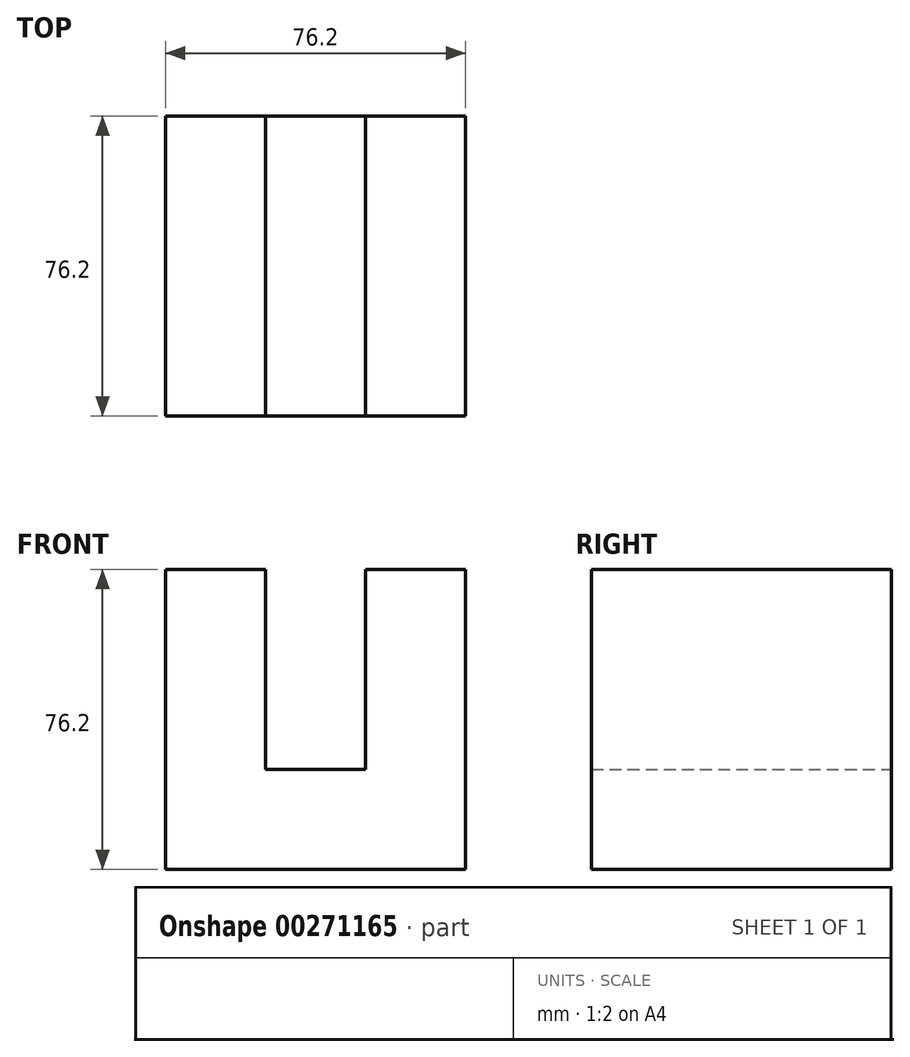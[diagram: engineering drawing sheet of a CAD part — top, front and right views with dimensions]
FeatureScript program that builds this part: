
annotation { "Feature Type Name" : "Feature", "Feature Type Description" : "" }
export const myFeature = defineFeature(function(context is Context, id is Id, definition is map)
    precondition{}
    {
        {
            var Q0;
            Q0=qCreatedBy(makeId("Front.planeOp"),FACE);
            var sketch = newSketch(context, id + "F0", { "sketchPlane" : qUnion([Q0])});
            skLineSegment(sketch, "E0", {"start": v(-36.1, 76.2) * mm, "end": v(-36.1, 0) * mm});
            skLineSegment(sketch, "E1", {"start": v(-36.1, 0) * mm, "end": v(40.1, 0) * mm});
            skLineSegment(sketch, "E2", {"start": v(40.1, 0) * mm, "end": v(40.1, 76.2) * mm});
            skLineSegment(sketch, "E3", {"start": v(40.1, 76.2) * mm, "end": v(14.7, 76.2) * mm});
            skLineSegment(sketch, "E4", {"start": v(14.7, 76.2) * mm, "end": v(14.7, 25.4) * mm});
            skLineSegment(sketch, "E5", {"start": v(14.7, 25.4) * mm, "end": v(-10.7, 25.4) * mm});
            skLineSegment(sketch, "E6", {"start": v(-10.7, 25.4) * mm, "end": v(-10.7, 76.2) * mm});
            skLineSegment(sketch, "E7", {"start": v(-10.7, 76.2) * mm, "end": v(-36.1, 76.2) * mm});
            skSolve(sketch);
        }
        {
            var Q0;
            Q0 = qSketchRegion(id + "F0", true);
            extrude(context, id + "F1", {"entities" : qUnion([Q0]), "depth" : 76.2 * mm});
        }
    });
